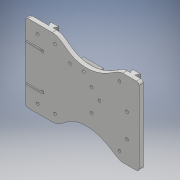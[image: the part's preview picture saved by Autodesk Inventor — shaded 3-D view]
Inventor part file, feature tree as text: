
AUTODESK INVENTOR PART (.ipt)
format: ipt  version: 2017 (Build 210142000, 142)  size: 293,376 bytes
history: native  units: mm
features: sketch x9, extrude x6, hole x3, chamfer x1, fillet x1
ambient origin geometry x8: Origin, YZ Plane, XZ Plane, XY Plane, X Axis, Y Axis, Z Axis, Center Point
bodies: Solid1 (feature_tree)
feature tree (20):
  extrude  "Extrusion1"  Depth=90.0mm
  sketch  "Sketch2"  dims[d2=20.0mm d3=41.0mm]
  extrude  "Extrusion7"  Depth=41.0mm
  extrude  "Extrusion3"  Depth=1.5mm
  extrude  "Extrusion4"  Depth=9.5mm
  extrude  "Extrusion5"  Depth=5.0mm
  hole  "Hole1"  [1 undecoded]
  hole  "Hole2"  [1 undecoded]
  chamfer  "Chamfer1"  Distance=36.0mm
  fillet  "Fillet1"  Radius=11.0mm
  hole  "Hole3"  [1 undecoded]
  extrude  "Extrusion8"  Depth=20.0mm
  sketch  "Sketch1"  dims[d0=132.0mm d1=90.0mm]
  sketch  "Sketch3"  dims[d4=1.5mm d5=1.5mm]
  sketch  "Sketch4"  dims[d6=5.0mm d7=0.0mm d8=9.5mm]
  sketch  "Sketch5"  dims[d10=22.0mm d11=5.0mm]
  sketch  "Sketch6"  dims[d15=4.5mm d23=120.0mm d24=0.0mm]
  sketch  "Sketch7"  dims[d25=3.0mm d26=70.0mm]
  sketch  "Sketch10"  dims[d27=3.0mm]
  sketch  "Sketch11"  dims[d28=20.0mm d29=36.0mm d30=11.0mm d31=0.0mm d32=2.0mm d33=0.0mm d34=20.0mm d35=16.0mm d41=5.0mm d42=5.0mm d45=3.0mm d46=6.0mm d47=4.0mm d48=2.0mm d49=90.0deg d50=8.0mm d51=20.594885mm d52=53.3mm d53=100.0mm d54=20.0mm d55=66.1mm d56=7.6mm d57=33.9mm d58=27.9mm d61=3.0mm d62=6.0mm d63=4.0mm d64=2.0mm d65=90.0deg d66=8.0mm d67=20.594885mm d68=0.5mm d69=2.0mm d70=45.0deg d71=3.0mm d81=50.1mm d82=2.5mm d83=16.0mm d84=4.0mm d86=43.145349mm d88=43.145349mm d90=60.0mm d91=10.0mm d92=0.0mm d93=45.0mm d94=22.5mm d95=22.5mm d100=10.0mm d101=10.0mm d102=10.0mm d103=10.0mm d104=10.0mm d105=10.0mm d106=10.0mm d107=10.0mm d108=3.0mm d109=6.0mm d110=4.0mm d111=2.0mm d112=90.0deg d113=8.0mm d114=20.594885mm d115=10.0mm d116=0.0mm d117=9.0mm]
note: 3 required parameter values undecoded (feature->parameter linkage not recoverable at this tier; creation-order binding heuristic only, values carry confidence <= 0.55)
